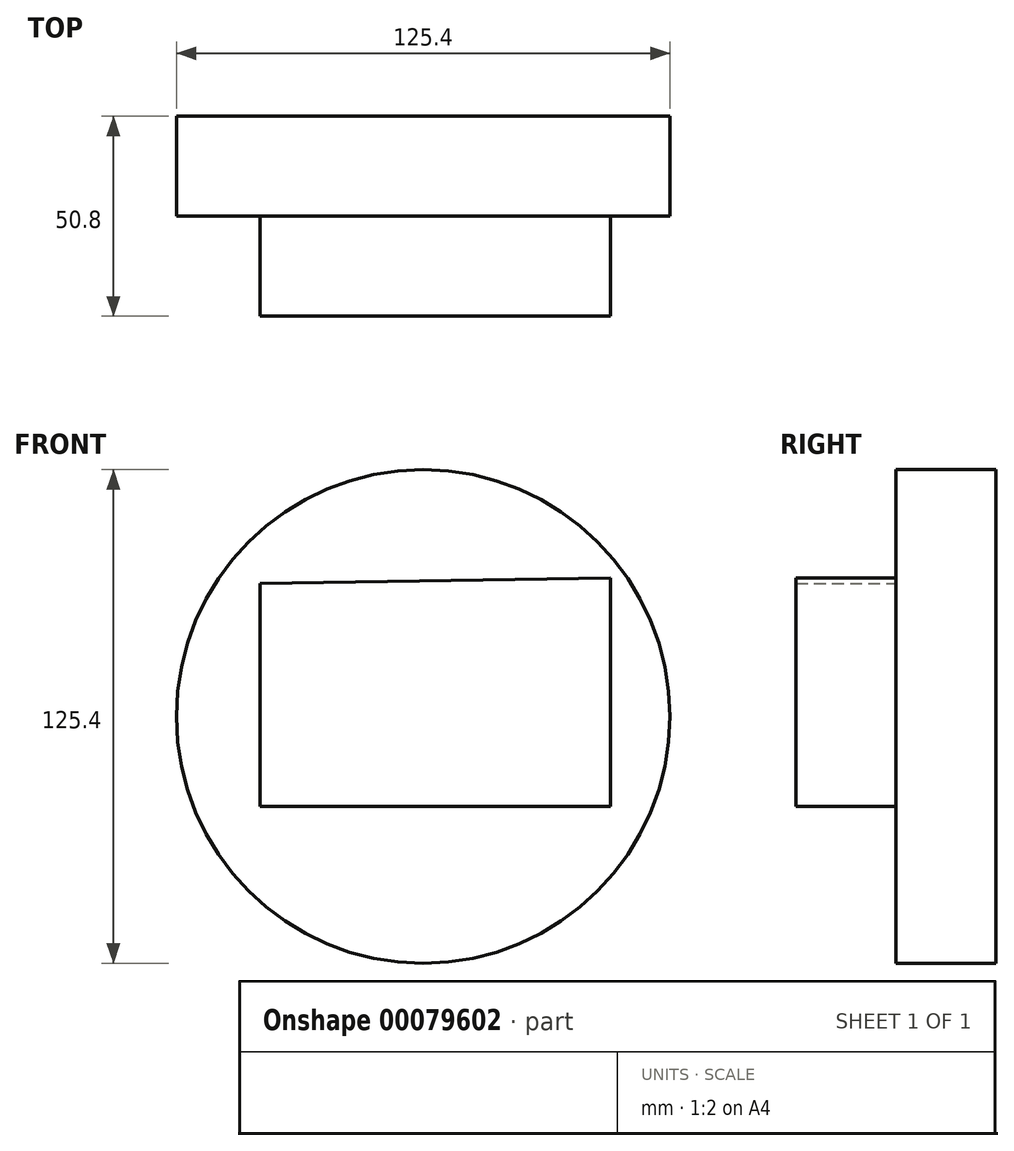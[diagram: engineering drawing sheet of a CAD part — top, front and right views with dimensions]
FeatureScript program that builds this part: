
annotation { "Feature Type Name" : "Feature", "Feature Type Description" : "" }
export const myFeature = defineFeature(function(context is Context, id is Id, definition is map)
    precondition{}
    {
        {
            var Q0;
            Q0=qCreatedBy(makeId("Front.planeOp"),FACE);
            var sketch = newSketch(context, id + "F0", { "sketchPlane" : qUnion([Q0])});
            skLineSegment(sketch, "E0", {"start": v(-52.4, 55.9) * mm, "end": v(-52.4, -55.07) * mm});
            skLineSegment(sketch, "E1", {"start": v(-52.4, -55.07) * mm, "end": v(47.92, 17.52) * mm});
            skLineSegment(sketch, "E2", {"start": v(47.92, 17.52) * mm, "end": v(-52.4, 55.9) * mm});
            skSolve(sketch);
        }
        {
            var Q0;
            Q0=makeQuery(id+"F0.imprint","IMPRINT",FACE,{"disambiguationData":[TD([[makeQuery(id+"F0.imprint","IMPRINT",EDGE,{"derivedFrom":sQuery(id+"F0.wireOp",EDGE,"E0")}),1.0]])]});
            extrude(context, id + "F1", {"entities" : qUnion([Q0]), "depth" : 0.03 * mm});
        }
        {
            var Q0;
            Q0=makeQuery(id+"F1.opExtrude","SWEPT_BODY",BODY,{"disambiguationData":[OSD([sQuery(id+"F0.wireOp",EDGE,"E0"),sQuery(id+"F0.wireOp",EDGE,"E1"),sQuery(id+"F0.wireOp",EDGE,"E2")])]});
            deleteBodies(context, id + "F2", {"entities" : qUnion([Q0])});
        }
        {
            var Q0;
            Q0=qCreatedBy(makeId("Front.planeOp"),FACE);
            var sketch = newSketch(context, id + "F3", { "sketchPlane" : qUnion([Q0])});
            skCircle(sketch, "E3", {"center": v(0, 0) * mm, "radius": 62.7 * mm});
            skSolve(sketch);
        }
        {
            var Q0;
            Q0=makeQuery(id+"F3.imprint","IMPRINT",FACE,{"disambiguationData":[TD([[makeQuery(id+"F3.imprint","IMPRINT",EDGE,{"derivedFrom":sQuery(id+"F3.wireOp",EDGE,"E3")}),1.0]])]});
            extrude(context, id + "F4", {"entities" : qUnion([Q0]), "depth" : 25.4 * mm});
        }
        {
            var Q0;
            Q0=makeQuery(id+"F4.opExtrude","CAP_FACE",FACE,{"disambiguationData":[OSD([sQuery(id+"F3.wireOp",EDGE,"E3")])],"isStart":false});
            var sketch = newSketch(context, id + "F5", { "sketchPlane" : qUnion([Q0])});
            skLineSegment(sketch, "E4", {"start": v(-41.48, 33.77) * mm, "end": v(-41.48, -22.84) * mm});
            skLineSegment(sketch, "E5", {"start": v(-41.48, -22.84) * mm, "end": v(47.64, -22.84) * mm});
            skLineSegment(sketch, "E6", {"start": v(47.64, -22.84) * mm, "end": v(47.64, 35.17) * mm});
            skLineSegment(sketch, "E7", {"start": v(47.64, 35.17) * mm, "end": v(-41.48, 33.77) * mm});
            skSolve(sketch);
        }
        {
            var Q0;
            Q0=makeQuery(id+"F5.imprint","IMPRINT",FACE,{"disambiguationData":[TD([[makeQuery(id+"F5.imprint","IMPRINT",EDGE,{"derivedFrom":sQuery(id+"F5.wireOp",EDGE,"E4")}),1.0]])]});
            extrude(context, id + "F6", {"entities" : qUnion([Q0]), "operationType" : NewBodyOperationType.ADD, "depth" : 25.4 * mm});
        }
    });
